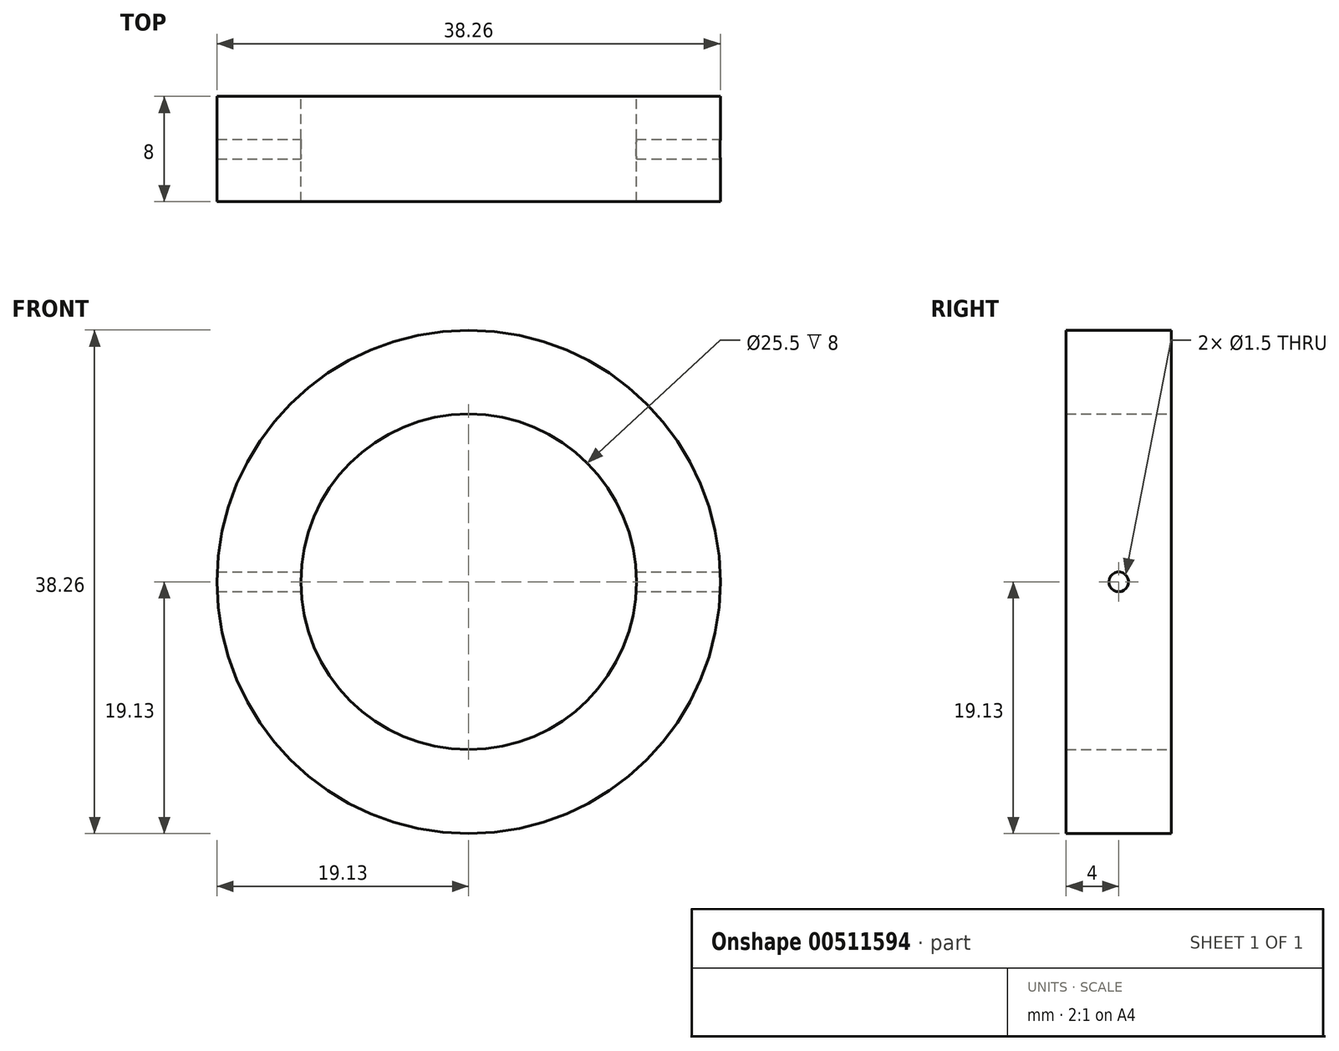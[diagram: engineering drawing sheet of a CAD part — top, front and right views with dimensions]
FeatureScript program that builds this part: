
annotation { "Feature Type Name" : "Feature", "Feature Type Description" : "" }
export const myFeature = defineFeature(function(context is Context, id is Id, definition is map)
    precondition{}
    {
        {
            var Q0;
            Q0=qCreatedBy(makeId("Front.planeOp"),FACE);
            var sketch = newSketch(context, id + "F0", { "sketchPlane" : qUnion([Q0])});
            skCircle(sketch, "E0", {"center": v(0, 0) * mm, "radius": 12.75 * mm});
            skCircle(sketch, "E1", {"center": v(0, 0) * mm, "radius": 19.12 * mm});
            skSolve(sketch);
        }
        {
            var Q0;
            Q0=makeQuery(id+"F0.imprint","IMPRINT",FACE,{"disambiguationData":[TD([[makeQuery(id+"F0.imprint","IMPRINT",EDGE,{"derivedFrom":sQuery(id+"F0.wireOp",EDGE,"E0")}),-1.0]])]});
            extrude(context, id + "F1", {"entities" : qUnion([Q0]), "depth" : 8 * mm, "offsetDistance" : 25 * mm});
        }
        {
            var Q0;
            Q0=qCreatedBy(makeId("Right.planeOp"),FACE);
            var sketch = newSketch(context, id + "F2", { "sketchPlane" : qUnion([Q0])});
            skCircle(sketch, "E2", {"center": v(-4, 0) * mm, "radius": 0.75 * mm});
            skSolve(sketch);
        }
        {
            var Q0;
            Q0=makeQuery(id+"F2.imprint","IMPRINT",FACE,{"disambiguationData":[TD([[makeQuery(id+"F2.imprint","IMPRINT",EDGE,{"derivedFrom":sQuery(id+"F2.wireOp",EDGE,"E2")}),1.0]])]});
            extrude(context, id + "F3", {"entities" : qUnion([Q0]), "operationType" : NewBodyOperationType.REMOVE, "oppositeDirection" : true, "depth" : 100 * mm, "offsetDistance" : 25 * mm, "symmetric" : true});
        }
    });
